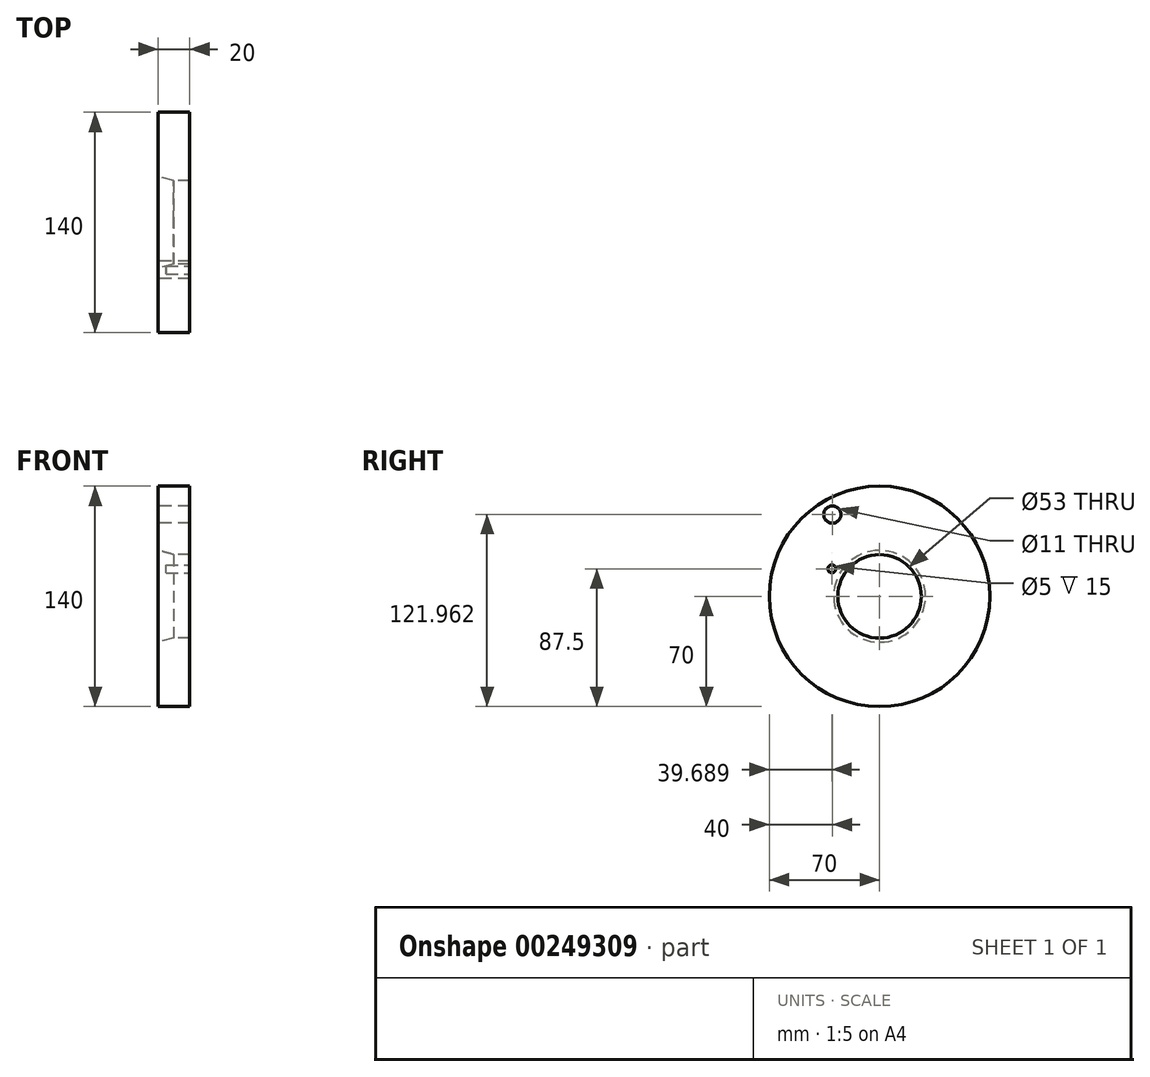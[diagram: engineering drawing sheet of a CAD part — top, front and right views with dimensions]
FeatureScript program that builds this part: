
annotation { "Feature Type Name" : "Feature", "Feature Type Description" : "" }
export const myFeature = defineFeature(function(context is Context, id is Id, definition is map)
    precondition{}
    {
        {
            var Q0;
            Q0=qCreatedBy(makeId("Front.planeOp"),FACE);
            var sketch = newSketch(context, id + "F0", { "sketchPlane" : qUnion([Q0])});
            skLineSegment(sketch, "E0", {"start": v(0, 29.15) * mm, "end": v(9.8, 26.5) * mm});
            skLineSegment(sketch, "E1", {"start": v(9.8, 26.5) * mm, "end": v(20, 26.5) * mm});
            skLineSegment(sketch, "E2", {"start": v(20, 26.5) * mm, "end": v(20, 70) * mm});
            skLineSegment(sketch, "E3", {"start": v(20, 70) * mm, "end": v(0, 70) * mm});
            skLineSegment(sketch, "E4", {"start": v(0, 70) * mm, "end": v(0, 29.15) * mm});
            skLineSegment(sketch, "E5", {"start": v(0, 0) * mm, "end": v(43.06, 0) * mm});
            skSolve(sketch);
        }
        {
            var Q0;
            Q0=makeQuery(id+"F0.imprint","IMPRINT",FACE,{"disambiguationData":[TD([[makeQuery(id+"F0.imprint","IMPRINT",EDGE,{"derivedFrom":sQuery(id+"F0.wireOp",EDGE,"E0")}),1.0]])]});
            var Q1;
            Q1=sQuery(id+"F0.wireOp",EDGE,"E5");
            revolve(context, id + "F1", {"entities" : qUnion([Q0]), "axis" : qUnion([Q1]), "revolveType" : RevolveType.FULL});
        }
        {
            var Q0;
            Q0=makeQuery(id+"F1.opRevolve","SWEPT_FACE",FACE,{"disambiguationData":[OSD([sQuery(id+"F0.wireOp",EDGE,"E4")])]});
            var sketch = newSketch(context, id + "F2", { "sketchPlane" : qUnion([Q0])});
            skLineSegment(sketch, "E6", {"start": v(0, 0) * mm, "end": v(30, 51.96) * mm, "construction": true});
            skCircle(sketch, "E7", {"center": v(30, 51.96) * mm, "radius": 5.5 * mm});
            skSolve(sketch);
        }
        {
            var Q0;
            Q0=makeQuery(id+"F2.imprint","IMPRINT",FACE,{"disambiguationData":[TD([[makeQuery(id+"F2.imprint","IMPRINT",EDGE,{"derivedFrom":sQuery(id+"F2.wireOp",EDGE,"E7")}),1.0]])]});
            extrude(context, id + "F3", {"entities" : qUnion([Q0]), "operationType" : NewBodyOperationType.REMOVE, "endBound" : BoundingType.THROUGH_ALL, "oppositeDirection" : true, "depth" : 25 * mm, "offsetDistance" : 25 * mm});
        }
        {
            var Q0;
            Q0=makeQuery(id+"F1.opRevolve","SWEPT_FACE",FACE,{"disambiguationData":[OSD([sQuery(id+"F0.wireOp",EDGE,"E2")])]});
            var sketch = newSketch(context, id + "F4", { "sketchPlane" : qUnion([Q0])});
            skCircle(sketch, "E8", {"center": v(-30.31, 17.5) * mm, "radius": 2.5 * mm});
            skLineSegment(sketch, "E9", {"start": v(0, 0) * mm, "end": v(-30.31, 17.5) * mm, "construction": true});
            skSolve(sketch);
        }
        {
            var Q0;
            Q0=makeQuery(id+"F4.imprint","IMPRINT",FACE,{"disambiguationData":[TD([[makeQuery(id+"F4.imprint","IMPRINT",EDGE,{"derivedFrom":sQuery(id+"F4.wireOp",EDGE,"E8")}),1.0]])]});
            extrude(context, id + "F5", {"entities" : qUnion([Q0]), "operationType" : NewBodyOperationType.REMOVE, "oppositeDirection" : true, "depth" : 15 * mm, "offsetDistance" : 25 * mm});
        }
    });
